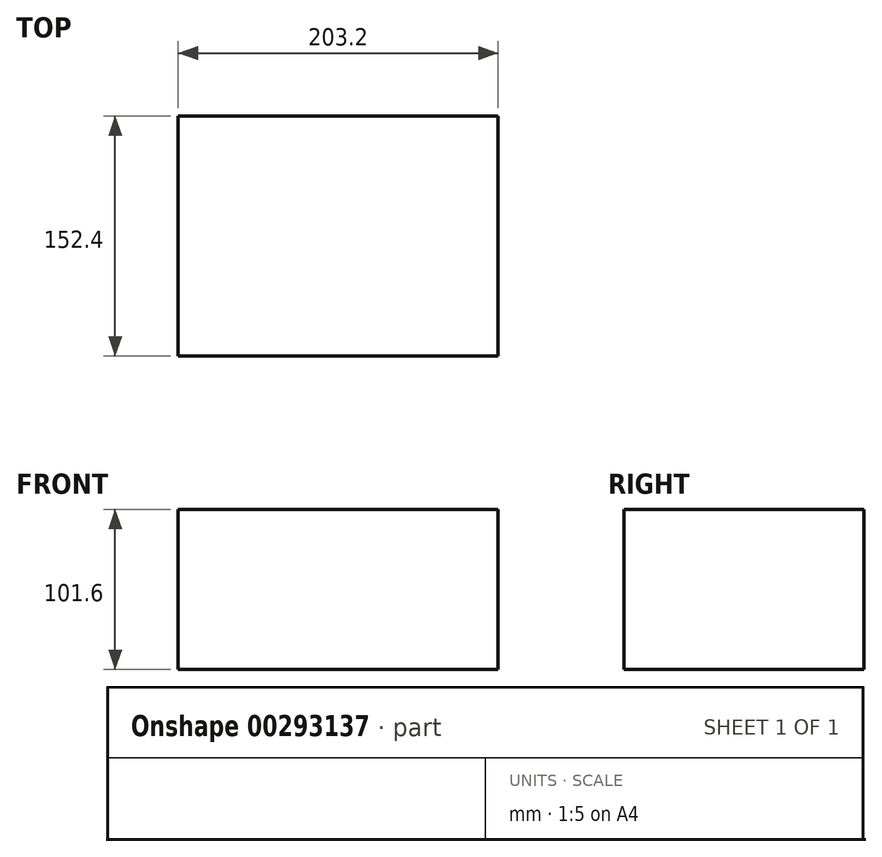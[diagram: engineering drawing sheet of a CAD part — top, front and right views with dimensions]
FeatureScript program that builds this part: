
annotation { "Feature Type Name" : "Feature", "Feature Type Description" : "" }
export const myFeature = defineFeature(function(context is Context, id is Id, definition is map)
    precondition{}
    {
        {
            var Q0;
            Q0=qCreatedBy(makeId("Front.planeOp"),FACE);
            var sketch = newSketch(context, id + "F0", { "sketchPlane" : qUnion([Q0])});
            skLineSegment(sketch, "E0", {"start": v(-53.12, 40.34) * mm, "end": v(-53.12, -61.26) * mm});
            skLineSegment(sketch, "E1", {"start": v(-53.12, -61.26) * mm, "end": v(150.08, -61.26) * mm});
            skLineSegment(sketch, "E2", {"start": v(150.08, -61.26) * mm, "end": v(150.08, 40.34) * mm});
            skLineSegment(sketch, "E3", {"start": v(150.08, 40.34) * mm, "end": v(-53.12, 40.34) * mm});
            skSolve(sketch);
        }
        {
            var Q0;
            Q0 = qSketchRegion(id + "F0", true);
            extrude(context, id + "F1", {"entities" : qUnion([Q0]), "depth" : 152.4 * mm, "offsetDistance" : 25.4 * mm});
        }
    });
